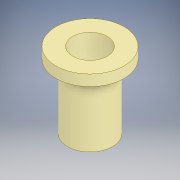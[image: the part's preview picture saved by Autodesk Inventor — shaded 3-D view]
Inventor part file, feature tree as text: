
AUTODESK INVENTOR PART (.ipt)
format: ipt  version: 2019 (Build 230136000, 136)  size: 110,080 bytes
history: native  units: mm
features: other x3, extrude x2, hole x1
ambient origin geometry x8: Origin, YZ Plane, XZ Plane, XY Plane, X Axis, Y Axis, Z Axis, Center Point
bodies: Solid1 (feature_tree)
feature tree (6):
  extrude  "Washer"  Depth=6.6mm
  extrude  "Shoulder"  Depth=9.53mm TaperAngle=0.0deg
  hole  "Screw Hole"  [1 undecoded]
  other  "Washer Cross Section"
  other  "Shoulder Cross Section"
  other  "Screw Hole Position"
note: 1 required parameter value undecoded (feature->parameter linkage not recoverable at this tier; creation-order binding heuristic only, values carry confidence <= 0.55)
